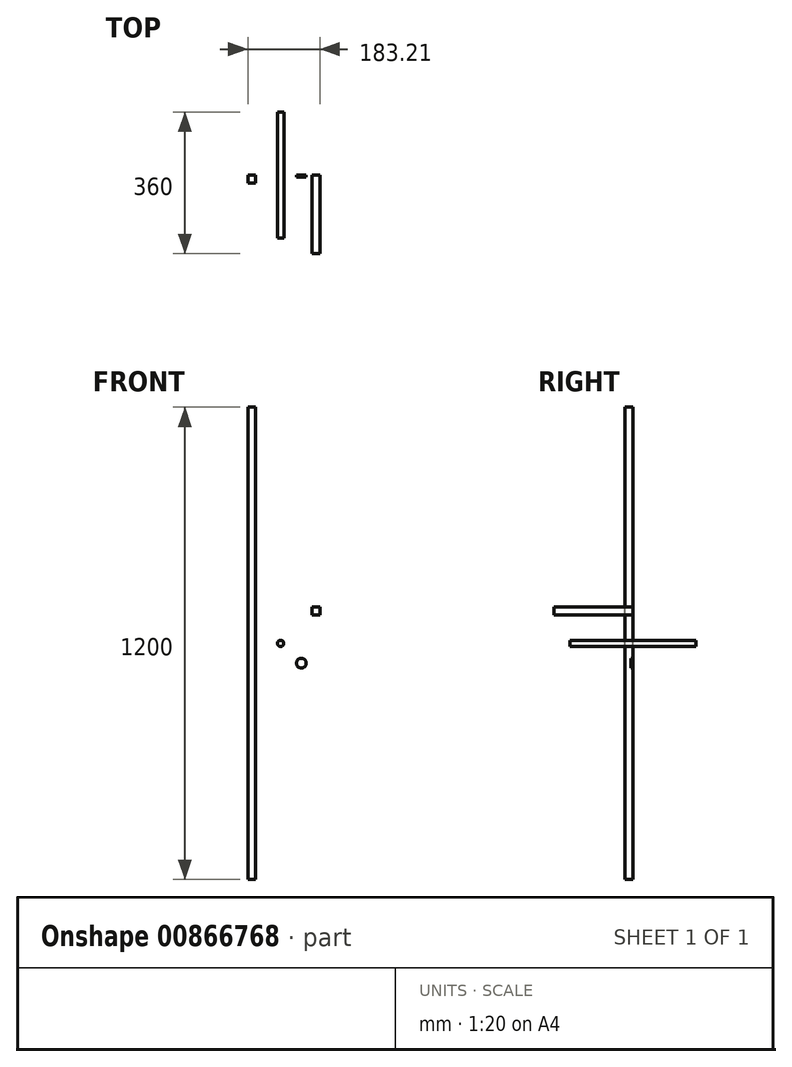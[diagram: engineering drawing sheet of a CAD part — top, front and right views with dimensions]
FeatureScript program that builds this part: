
annotation { "Feature Type Name" : "Feature", "Feature Type Description" : "" }
export const myFeature = defineFeature(function(context is Context, id is Id, definition is map)
    precondition{}
    {
        {
            var Q0;
            Q0=qCreatedBy(makeId("Front.planeOp"),FACE);
            var sketch = newSketch(context, id + "F0", { "sketchPlane" : qUnion([Q0])});
            skCircle(sketch, "E0", {"center": v(0, 0) * mm, "radius": 8 * mm});
            skSolve(sketch);
        }
        {
            var Q0;
            Q0=makeQuery(id+"F0.imprint","IMPRINT",FACE,{"disambiguationData":[TD([[makeQuery(id+"F0.imprint","IMPRINT",EDGE,{"derivedFrom":sQuery(id+"F0.wireOp",EDGE,"E0")}),1.0]])]});
            extrude(context, id + "F1", {"entities" : qUnion([Q0]), "endBound" : BoundingType.SYMMETRIC, "depth" : 320 * mm, "offsetDistance" : 25 * mm});
        }
        {
            var Q0;
            Q0=qCreatedBy(makeId("Front.planeOp"),FACE);
            var sketch = newSketch(context, id + "F2", { "sketchPlane" : qUnion([Q0])});
            skLineSegment(sketch, "E1.bottom", {"start": v(-63.32, -600) * mm, "end": v(-83.32, -600) * mm});
            skLineSegment(sketch, "E1.top", {"start": v(-63.32, 600) * mm, "end": v(-83.32, 600) * mm});
            skLineSegment(sketch, "E1.left", {"start": v(-63.32, -600) * mm, "end": v(-63.32, 600) * mm});
            skLineSegment(sketch, "E1.right", {"start": v(-83.32, -600) * mm, "end": v(-83.32, 600) * mm});
            skPoint(sketch, "E1.middle", {"position": v(-73.32, 0) * mm});
            skSolve(sketch);
        }
        {
            var Q0;
            Q0=makeQuery(id+"F2.imprint","IMPRINT",FACE,{"disambiguationData":[TD([[makeQuery(id+"F2.imprint","IMPRINT",EDGE,{"derivedFrom":sQuery(id+"F2.wireOp",EDGE,"E1.bottom")}),-1.0]])]});
            extrude(context, id + "F3", {"entities" : qUnion([Q0]), "depth" : 20 * mm, "offsetDistance" : 25 * mm});
        }
        {
            var Q0;
            Q0=qCreatedBy(makeId("Front.planeOp"),FACE);
            var sketch = newSketch(context, id + "F4", { "sketchPlane" : qUnion([Q0])});
            skLineSegment(sketch, "E2.bottom", {"start": v(99.89, 72.1) * mm, "end": v(79.89, 72.1) * mm});
            skLineSegment(sketch, "E2.top", {"start": v(99.89, 92.1) * mm, "end": v(79.89, 92.1) * mm});
            skLineSegment(sketch, "E2.left", {"start": v(99.89, 72.1) * mm, "end": v(99.89, 92.1) * mm});
            skLineSegment(sketch, "E2.right", {"start": v(79.89, 72.1) * mm, "end": v(79.89, 92.1) * mm});
            skPoint(sketch, "E2.middle", {"position": v(89.89, 82.1) * mm});
            skSolve(sketch);
        }
        {
            var Q0;
            Q0=makeQuery(id+"F4.imprint","IMPRINT",FACE,{"disambiguationData":[TD([[makeQuery(id+"F4.imprint","IMPRINT",EDGE,{"derivedFrom":sQuery(id+"F4.wireOp",EDGE,"E2.bottom")}),-1.0]])]});
            extrude(context, id + "F5", {"entities" : qUnion([Q0]), "depth" : 200 * mm, "offsetDistance" : 25 * mm});
        }
        {
            var Q0;
            Q0=qCreatedBy(makeId("Front.planeOp"),FACE);
            var sketch = newSketch(context, id + "F6", { "sketchPlane" : qUnion([Q0])});
            skCircle(sketch, "E3", {"center": v(52.6, -50.26) * mm, "radius": 12.5 * mm});
            skSolve(sketch);
        }
        {
            var Q0;
            Q0=makeQuery(id+"F6.imprint","IMPRINT",FACE,{"disambiguationData":[TD([[makeQuery(id+"F6.imprint","IMPRINT",EDGE,{"derivedFrom":sQuery(id+"F6.wireOp",EDGE,"E3")}),1.0]])]});
            extrude(context, id + "F7", {"entities" : qUnion([Q0]), "depth" : 5 * mm, "offsetDistance" : 25 * mm});
        }
    });
